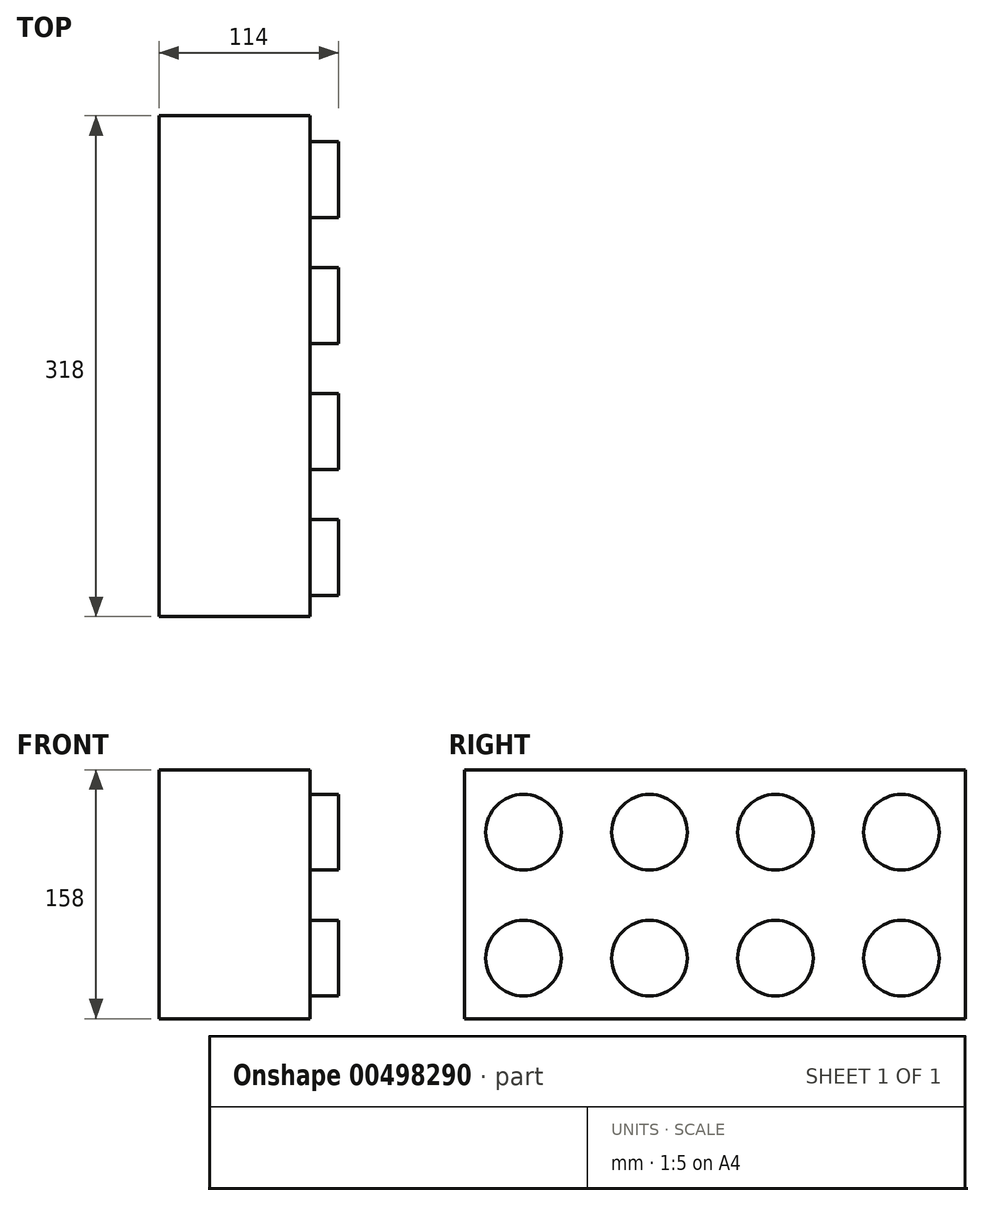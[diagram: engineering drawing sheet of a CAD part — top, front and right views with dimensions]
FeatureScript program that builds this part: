
annotation { "Feature Type Name" : "Feature", "Feature Type Description" : "" }
export const myFeature = defineFeature(function(context is Context, id is Id, definition is map)
    precondition{}
    {
        {
            var Q0;
            Q0=qCreatedBy(makeId("Right.planeOp"),FACE);
            var sketch = newSketch(context, id + "F0", { "sketchPlane" : qUnion([Q0])});
            skLineSegment(sketch, "E0.bottom", {"start": v(0, 0) * mm, "end": v(318, 0) * mm});
            skLineSegment(sketch, "E0.top", {"start": v(0, 158) * mm, "end": v(318, 158) * mm});
            skLineSegment(sketch, "E0.left", {"start": v(0, 0) * mm, "end": v(0, 158) * mm});
            skLineSegment(sketch, "E0.right", {"start": v(318, 0) * mm, "end": v(318, 158) * mm});
            skSolve(sketch);
        }
        {
            var Q0;
            Q0=makeQuery(id+"F0.imprint","IMPRINT",FACE,{"disambiguationData":[TD([[makeQuery(id+"F0.imprint","IMPRINT",EDGE,{"derivedFrom":sQuery(id+"F0.wireOp",EDGE,"E0.bottom")}),1.0]])]});
            extrude(context, id + "F1", {"entities" : qUnion([Q0]), "depth" : 96 * mm});
        }
        {
            var Q0;
            Q0=makeQuery(id+"F1.opExtrude","CAP_FACE",FACE,{"disambiguationData":[OSD([sQuery(id+"F0.wireOp",EDGE,"E0.bottom"),sQuery(id+"F0.wireOp",EDGE,"E0.top"),sQuery(id+"F0.wireOp",EDGE,"E0.left"),sQuery(id+"F0.wireOp",EDGE,"E0.right")])],"isStart":false});
            var sketch = newSketch(context, id + "F2", { "sketchPlane" : qUnion([Q0])});
            skCircle(sketch, "E1", {"center": v(37.44, 38.44) * mm, "radius": 24 * mm});
            skCircle(sketch, "E2.0.1.0", {"center": v(37.44, 118.44) * mm, "radius": 24 * mm});
            skCircle(sketch, "E2.1.0.0", {"center": v(117.44, 38.44) * mm, "radius": 24 * mm});
            skCircle(sketch, "E2.1.1.0", {"center": v(117.44, 118.44) * mm, "radius": 24 * mm});
            skCircle(sketch, "E2.2.0.0", {"center": v(197.44, 38.44) * mm, "radius": 24 * mm});
            skCircle(sketch, "E2.2.1.0", {"center": v(197.44, 118.44) * mm, "radius": 24 * mm});
            skCircle(sketch, "E2.3.0.0", {"center": v(277.44, 38.44) * mm, "radius": 24 * mm});
            skCircle(sketch, "E2.3.1.0", {"center": v(277.44, 118.44) * mm, "radius": 24 * mm});
            skLineSegment(sketch, "E2.direction1", {"start": v(37.44, 38.44) * mm, "end": v(117.44, 38.44) * mm, "construction": true});
            skLineSegment(sketch, "E2.direction2", {"start": v(37.44, 38.44) * mm, "end": v(37.44, 118.44) * mm, "construction": true});
            skSolve(sketch);
        }
        {
            var Q0;
            Q0=makeQuery(id+"F2.imprint","IMPRINT",FACE,{"disambiguationData":[TD([[makeQuery(id+"F2.imprint","IMPRINT",EDGE,{"derivedFrom":sQuery(id+"F2.wireOp",EDGE,"E2.0.1.0")}),1.0]])]});
            var Q1;
            Q1=makeQuery(id+"F2.imprint","IMPRINT",FACE,{"disambiguationData":[TD([[makeQuery(id+"F2.imprint","IMPRINT",EDGE,{"derivedFrom":sQuery(id+"F2.wireOp",EDGE,"E2.1.1.0")}),1.0]])]});
            var Q2;
            Q2=makeQuery(id+"F2.imprint","IMPRINT",FACE,{"disambiguationData":[TD([[makeQuery(id+"F2.imprint","IMPRINT",EDGE,{"derivedFrom":sQuery(id+"F2.wireOp",EDGE,"E2.2.1.0")}),1.0]])]});
            var Q3;
            Q3=makeQuery(id+"F2.imprint","IMPRINT",FACE,{"disambiguationData":[TD([[makeQuery(id+"F2.imprint","IMPRINT",EDGE,{"derivedFrom":sQuery(id+"F2.wireOp",EDGE,"E2.3.1.0")}),1.0]])]});
            var Q4;
            Q4=makeQuery(id+"F2.imprint","IMPRINT",FACE,{"disambiguationData":[TD([[makeQuery(id+"F2.imprint","IMPRINT",EDGE,{"derivedFrom":sQuery(id+"F2.wireOp",EDGE,"E2.3.0.0")}),1.0]])]});
            var Q5;
            Q5=makeQuery(id+"F2.imprint","IMPRINT",FACE,{"disambiguationData":[TD([[makeQuery(id+"F2.imprint","IMPRINT",EDGE,{"derivedFrom":sQuery(id+"F2.wireOp",EDGE,"E2.2.0.0")}),1.0]])]});
            var Q6;
            Q6=makeQuery(id+"F2.imprint","IMPRINT",FACE,{"disambiguationData":[TD([[makeQuery(id+"F2.imprint","IMPRINT",EDGE,{"derivedFrom":sQuery(id+"F2.wireOp",EDGE,"E2.1.0.0")}),1.0]])]});
            var Q7;
            Q7=makeQuery(id+"F2.imprint","IMPRINT",FACE,{"disambiguationData":[TD([[makeQuery(id+"F2.imprint","IMPRINT",EDGE,{"derivedFrom":sQuery(id+"F2.wireOp",EDGE,"E1")}),1.0]])]});
            extrude(context, id + "F3", {"entities" : qUnion([Q0, Q1, Q2, Q3, Q4, Q5, Q6, Q7]), "operationType" : NewBodyOperationType.ADD, "depth" : 18 * mm});
        }
    });
